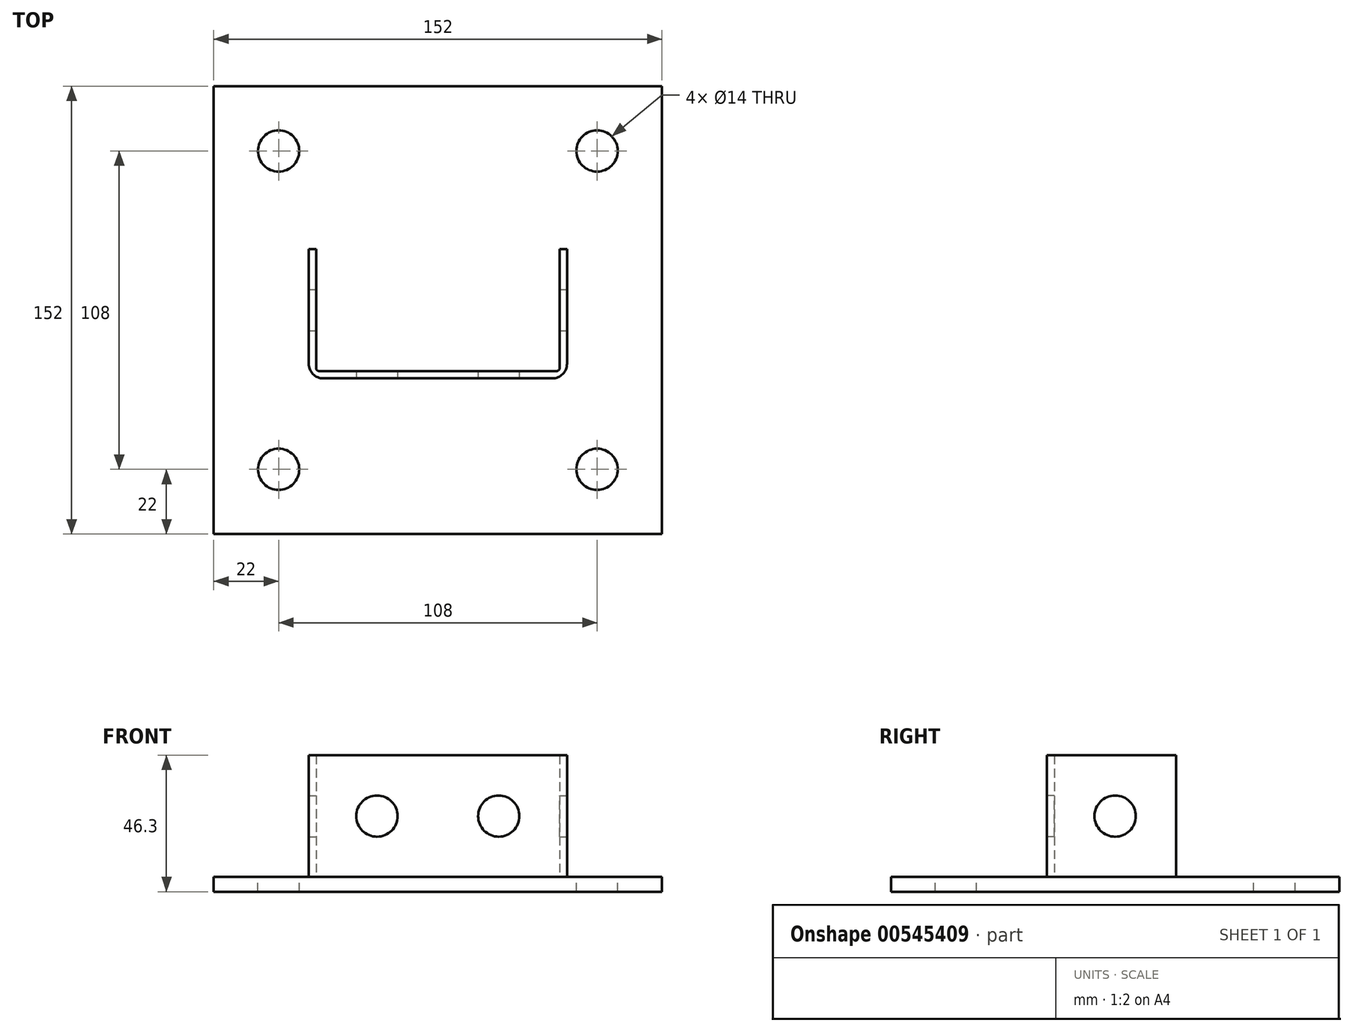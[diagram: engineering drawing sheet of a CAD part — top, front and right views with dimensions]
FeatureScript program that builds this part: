
annotation { "Feature Type Name" : "Feature", "Feature Type Description" : "" }
export const myFeature = defineFeature(function(context is Context, id is Id, definition is map)
    precondition{}
    {
        {
            var Q0;
            Q0=qCreatedBy(makeId("Top.planeOp"),FACE);
            var sketch = newSketch(context, id + "F0", { "sketchPlane" : qUnion([Q0])});
            skLineSegment(sketch, "E0.bottom", {"start": v(-76, 76) * mm, "end": v(76, 76) * mm});
            skLineSegment(sketch, "E0.top", {"start": v(-76, -76) * mm, "end": v(76, -76) * mm});
            skLineSegment(sketch, "E0.left", {"start": v(-76, 76) * mm, "end": v(-76, -76) * mm});
            skLineSegment(sketch, "E0.right", {"start": v(76, 76) * mm, "end": v(76, -76) * mm});
            skCircle(sketch, "E1", {"center": v(-54, 54) * mm, "radius": 7 * mm});
            skCircle(sketch, "E2", {"center": v(54, 54) * mm, "radius": 7 * mm});
            skCircle(sketch, "E3", {"center": v(-54, -54) * mm, "radius": 7 * mm});
            skCircle(sketch, "E4", {"center": v(54, -54) * mm, "radius": 7 * mm});
            skSolve(sketch);
        }
        {
            var Q0;
            Q0=makeQuery(id+"F0.imprint","IMPRINT",FACE,{"disambiguationData":[TD([[makeQuery(id+"F0.imprint","IMPRINT",EDGE,{"derivedFrom":sQuery(id+"F0.wireOp",EDGE,"E0.bottom")}),-1.0]])]});
            extrude(context, id + "F1", {"entities" : qUnion([Q0]), "oppositeDirection" : true, "depth" : 5 * mm, "offsetDistance" : 25 * mm});
        }
        {
            var Q0;
            Q0=makeQuery(id+"F1.opExtrude","CAP_FACE",FACE,{"disambiguationData":[OSD([sQuery(id+"F0.wireOp",EDGE,"E0.bottom"),sQuery(id+"F0.wireOp",EDGE,"E0.top"),sQuery(id+"F0.wireOp",EDGE,"E0.left"),sQuery(id+"F0.wireOp",EDGE,"E0.right")])],"isStart":true});
            var sketch = newSketch(context, id + "F2", { "sketchPlane" : qUnion([Q0])});
            skLineSegment(sketch, "E5", {"start": v(-43.8, 20.65) * mm, "end": v(-43.8, -23.15) * mm});
            skLineSegment(sketch, "E6", {"start": v(-43.8, -23.15) * mm, "end": v(43.8, -23.15) * mm});
            skLineSegment(sketch, "E7", {"start": v(43.8, -23.15) * mm, "end": v(43.8, 20.65) * mm});
            skLineSegment(sketch, "E8", {"start": v(43.8, 20.65) * mm, "end": v(41.3, 20.65) * mm});
            skLineSegment(sketch, "E9", {"start": v(41.3, 20.65) * mm, "end": v(41.3, -20.65) * mm});
            skLineSegment(sketch, "E10", {"start": v(41.3, -20.65) * mm, "end": v(-41.3, -20.65) * mm});
            skLineSegment(sketch, "E11", {"start": v(-41.3, -20.65) * mm, "end": v(-41.3, 20.65) * mm});
            skLineSegment(sketch, "E12", {"start": v(-41.3, 20.65) * mm, "end": v(-43.8, 20.65) * mm});
            skSolve(sketch);
        }
        {
            var Q0;
            Q0 = qSketchRegion(id + "F2", true);
            extrude(context, id + "F3", {"entities" : qUnion([Q0]), "operationType" : NewBodyOperationType.ADD, "depth" : 41.3 * mm, "offsetDistance" : 25 * mm});
        }
        {
            var Q0;
            Q0=makeQuery(id+"F3.opExtrude","SWEPT_EDGE",EDGE,{"disambiguationData":[OSD([sQuery(id+"F2.wireOp",EDGE,"E6"),sQuery(id+"F2.wireOp",EDGE,"E7")])]});
            var Q1;
            Q1=makeQuery(id+"F3.opExtrude","SWEPT_EDGE",EDGE,{"disambiguationData":[OSD([sQuery(id+"F2.wireOp",EDGE,"E5"),sQuery(id+"F2.wireOp",EDGE,"E6")])]});
            fillet(context, id + "F4", {"entities" : qUnion([Q0, Q1]), "radius" : 5 * mm, "tangentPropagation" : true, "allowEdgeOverflow" : false});
        }
        {
            var Q0;
            Q0=makeQuery(id+"F3.opExtrude","SWEPT_EDGE",EDGE,{"disambiguationData":[OSD([sQuery(id+"F2.wireOp",EDGE,"E9"),sQuery(id+"F2.wireOp",EDGE,"E10")])]});
            var Q1;
            Q1=makeQuery(id+"F3.opExtrude","SWEPT_EDGE",EDGE,{"disambiguationData":[OSD([sQuery(id+"F2.wireOp",EDGE,"E10"),sQuery(id+"F2.wireOp",EDGE,"E11")])]});
            fillet(context, id + "F5", {"entities" : qUnion([Q0, Q1]), "radius" : 1 * mm, "tangentPropagation" : true, "allowEdgeOverflow" : false});
        }
        {
            var Q0;
            Q0=makeQuery(id+"F3.opExtrude","SWEPT_FACE",FACE,{"disambiguationData":[OSD([sQuery(id+"F2.wireOp",EDGE,"E7")])]});
            var sketch = newSketch(context, id + "F6", { "sketchPlane" : qUnion([Q0])});
            skCircle(sketch, "E13", {"center": v(0, 20.65) * mm, "radius": 7 * mm});
            skSolve(sketch);
        }
        {
            var Q0;
            Q0=sQuery(id+"F6.wireOp",VERTEX,"E13.center");
            var Q1;
            Q1=makeQuery(id+"F1.opExtrude","SWEPT_BODY",BODY,{"disambiguationData":[OSD([sQuery(id+"F0.wireOp",EDGE,"E0.bottom"),sQuery(id+"F0.wireOp",EDGE,"E0.top"),sQuery(id+"F0.wireOp",EDGE,"E0.left"),sQuery(id+"F0.wireOp",EDGE,"E0.right"),sQuery(id+"F0.wireOp",EDGE,"E1"),sQuery(id+"F0.wireOp",EDGE,"E2"),sQuery(id+"F0.wireOp",EDGE,"E3"),sQuery(id+"F0.wireOp",EDGE,"E4")])]});
            hole(context, id + "F7", {"style" : HoleStyle.SIMPLE, "endStyle" : HoleEndStyle.THROUGH, "holeDiameter" : 14 * mm, "tappedDepth" : 12 * mm, "tapClearance" : 3, "locations" : qUnion([Q0]), "scope" : qUnion([Q1])});
        }
        {
            var Q0;
            Q0=makeQuery(id+"F3.opExtrude","SWEPT_FACE",FACE,{"disambiguationData":[OSD([sQuery(id+"F2.wireOp",EDGE,"E6")])]});
            var sketch = newSketch(context, id + "F8", { "sketchPlane" : qUnion([Q0])});
            skCircle(sketch, "E14", {"center": v(-20.65, 20.65) * mm, "radius": 5.1 * mm});
            skCircle(sketch, "E15", {"center": v(20.65, 20.65) * mm, "radius": 5.73 * mm});
            skSolve(sketch);
        }
        {
            var Q0;
            Q0=sQuery(id+"F8.wireOp",VERTEX,"E14.center");
            var Q1;
            Q1=sQuery(id+"F8.wireOp",VERTEX,"E15.center");
            var Q2;
            Q2=makeQuery(id+"F1.opExtrude","SWEPT_BODY",BODY,{"disambiguationData":[OSD([sQuery(id+"F0.wireOp",EDGE,"E0.bottom"),sQuery(id+"F0.wireOp",EDGE,"E0.top"),sQuery(id+"F0.wireOp",EDGE,"E0.left"),sQuery(id+"F0.wireOp",EDGE,"E0.right"),sQuery(id+"F0.wireOp",EDGE,"E1"),sQuery(id+"F0.wireOp",EDGE,"E2"),sQuery(id+"F0.wireOp",EDGE,"E3"),sQuery(id+"F0.wireOp",EDGE,"E4")])]});
            hole(context, id + "F9", {"style" : HoleStyle.SIMPLE, "endStyle" : HoleEndStyle.THROUGH, "holeDiameter" : 14 * mm, "tappedDepth" : 12 * mm, "tapClearance" : 3, "locations" : qUnion([Q0, Q1]), "scope" : qUnion([Q2])});
        }
    });
